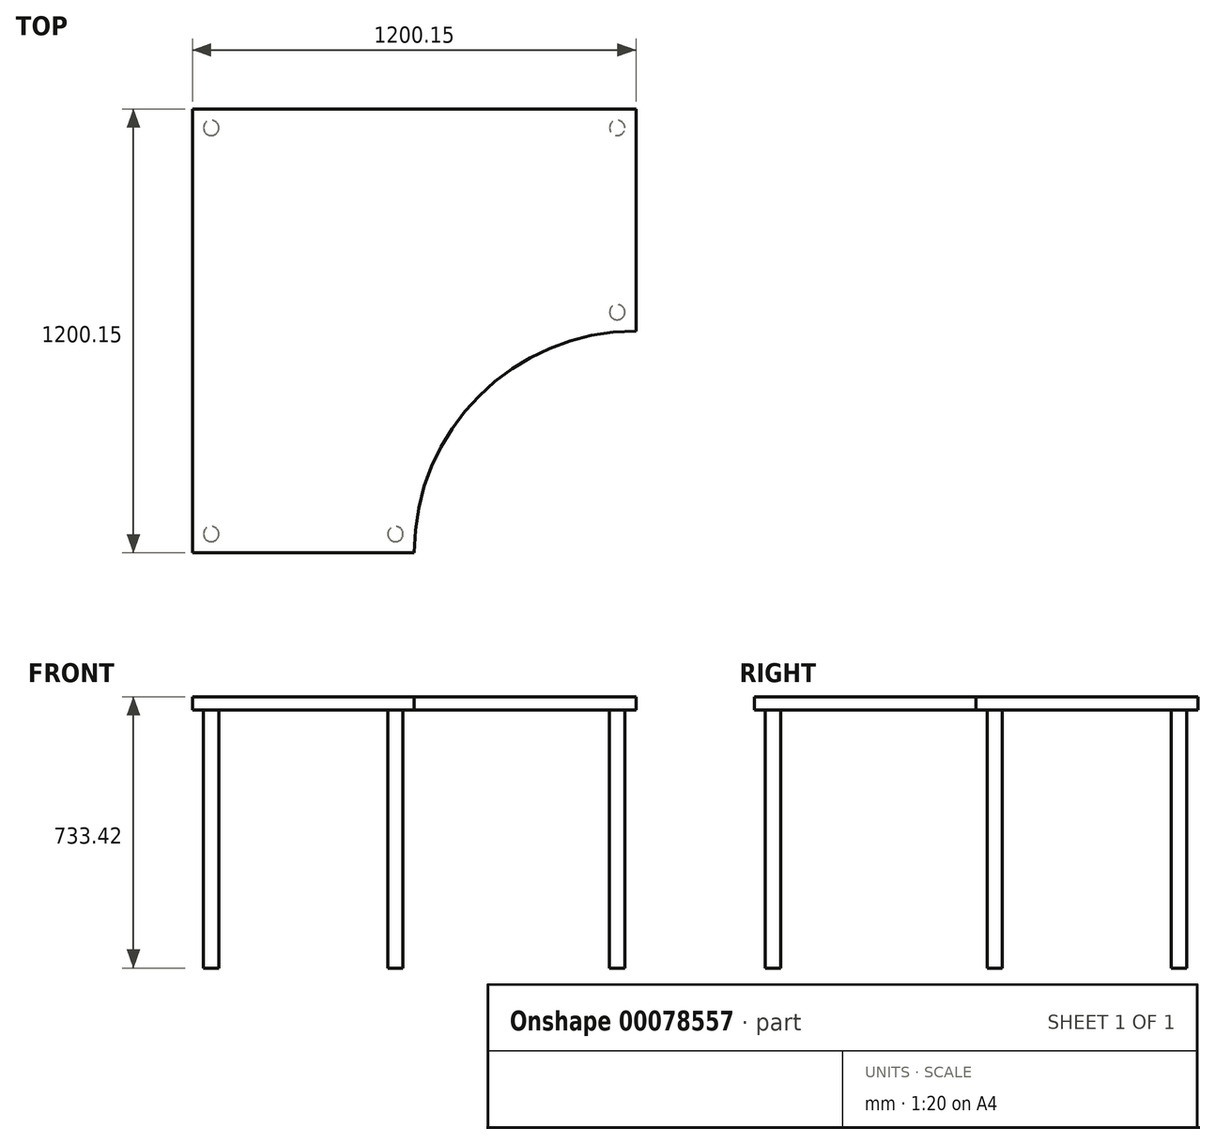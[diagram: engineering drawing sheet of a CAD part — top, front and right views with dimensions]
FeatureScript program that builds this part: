
annotation { "Feature Type Name" : "Feature", "Feature Type Description" : "" }
export const myFeature = defineFeature(function(context is Context, id is Id, definition is map)
    precondition{}
    {
        {
            var Q0;
            Q0=qCreatedBy(makeId("Top.planeOp"),FACE);
            var sketch = newSketch(context, id + "F0", { "sketchPlane" : qUnion([Q0])});
            skLineSegment(sketch, "E0.bottom", {"start": v(588.39, 824.32) * mm, "end": v(-611.76, 824.32) * mm});
            skLineSegment(sketch, "E0.top", {"start": v(588.39, -375.83) * mm, "end": v(-611.76, -375.83) * mm});
            skLineSegment(sketch, "E0.left", {"start": v(588.39, 824.32) * mm, "end": v(588.39, -375.83) * mm});
            skLineSegment(sketch, "E0.right", {"start": v(-611.76, 824.32) * mm, "end": v(-611.76, -375.83) * mm});
            skCircle(sketch, "E1", {"center": v(588.39, -375.83) * mm, "radius": 600.08 * mm});
            skSolve(sketch);
        }
        {
            var Q0;
            {var subQ2=sQuery(id+"F0.wireOp",EDGE,"E0.bottom");Q0=makeQuery(id+"F0.imprint","IMPRINT",FACE,{"disambiguationData":[TD([[makeQuery(id+"F0.imprint","IMPRINT",EDGE,{"derivedFrom":subQ2}),1.0]])]});}
            extrude(context, id + "F1", {"entities" : qUnion([Q0]), "depth" : 34.92 * mm});
        }
        {
            var Q0;
            Q0=makeQuery(id+"F1.opExtrude","CAP_FACE",FACE,{"disambiguationData":[OSD([sQuery(id+"F0.wireOp",EDGE,"E0.bottom"),sQuery(id+"F0.wireOp",EDGE,"E0.top"),sQuery(id+"F0.wireOp",EDGE,"E0.left"),sQuery(id+"F0.wireOp",EDGE,"E0.right"),sQuery(id+"F0.wireOp",EDGE,"E1")])],"isStart":true});
            var sketch = newSketch(context, id + "F2", { "sketchPlane" : qUnion([Q0])});
            skCircle(sketch, "E2", {"center": v(537.59, -773.52) * mm, "radius": 20.64 * mm});
            skCircle(sketch, "E3", {"center": v(-560.96, -773.52) * mm, "radius": 20.64 * mm});
            skCircle(sketch, "E4", {"center": v(-560.96, 325.03) * mm, "radius": 20.64 * mm});
            skCircle(sketch, "E5", {"center": v(537.59, -275.05) * mm, "radius": 20.64 * mm});
            skCircle(sketch, "E6", {"center": v(-62.49, 325.03) * mm, "radius": 20.64 * mm});
            skSolve(sketch);
        }
        {
            var Q0;
            Q0=makeQuery(id+"F2.imprint","IMPRINT",FACE,{"disambiguationData":[TD([[makeQuery(id+"F2.imprint","IMPRINT",EDGE,{"derivedFrom":sQuery(id+"F2.wireOp",EDGE,"E6")}),1.0]])]});
            var Q1;
            Q1=makeQuery(id+"F2.imprint","IMPRINT",FACE,{"disambiguationData":[TD([[makeQuery(id+"F2.imprint","IMPRINT",EDGE,{"derivedFrom":sQuery(id+"F2.wireOp",EDGE,"E4")}),1.0]])]});
            var Q2;
            Q2=makeQuery(id+"F2.imprint","IMPRINT",FACE,{"disambiguationData":[TD([[makeQuery(id+"F2.imprint","IMPRINT",EDGE,{"derivedFrom":sQuery(id+"F2.wireOp",EDGE,"E3")}),1.0]])]});
            var Q3;
            Q3=makeQuery(id+"F2.imprint","IMPRINT",FACE,{"disambiguationData":[TD([[makeQuery(id+"F2.imprint","IMPRINT",EDGE,{"derivedFrom":sQuery(id+"F2.wireOp",EDGE,"E2")}),1.0]])]});
            var Q4;
            Q4=makeQuery(id+"F2.imprint","IMPRINT",FACE,{"disambiguationData":[TD([[makeQuery(id+"F2.imprint","IMPRINT",EDGE,{"derivedFrom":sQuery(id+"F2.wireOp",EDGE,"E5")}),1.0]])]});
            extrude(context, id + "F3", {"entities" : qUnion([Q0, Q1, Q2, Q3, Q4]), "operationType" : NewBodyOperationType.ADD, "depth" : 698.5 * mm});
        }
    });
